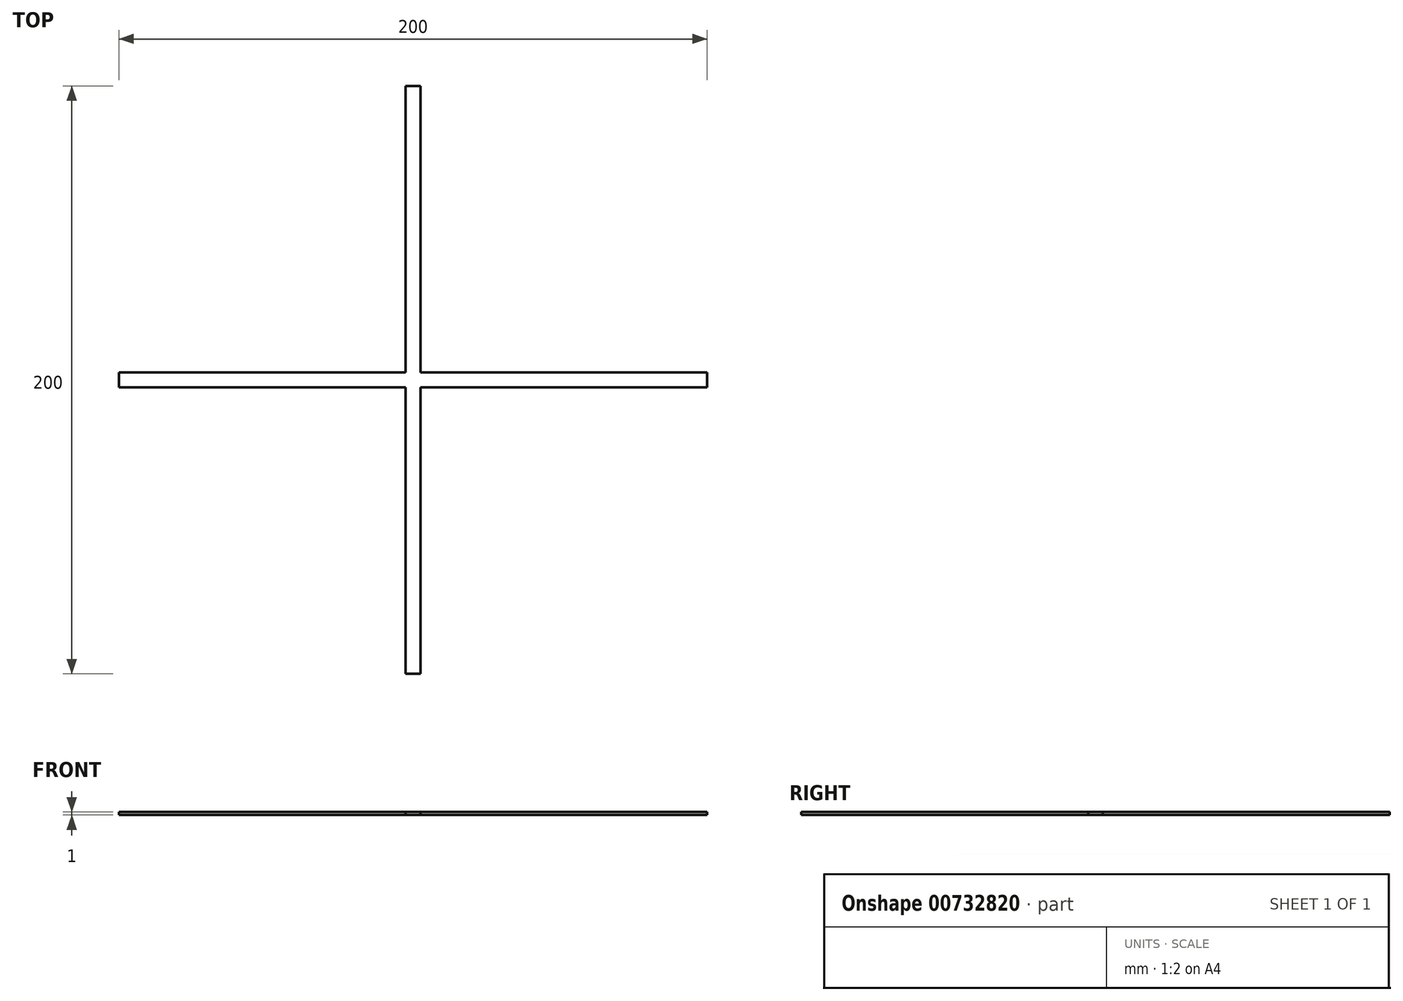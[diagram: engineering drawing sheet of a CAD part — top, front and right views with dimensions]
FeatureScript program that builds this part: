
annotation { "Feature Type Name" : "Feature", "Feature Type Description" : "" }
export const myFeature = defineFeature(function(context is Context, id is Id, definition is map)
    precondition{}
    {
        {
            var Q0;
            Q0=qCreatedBy(makeId("Top.planeOp"),FACE);
            var sketch = newSketch(context, id + "F0", { "sketchPlane" : qUnion([Q0])});
            skLineSegment(sketch, "E0.bottom", {"start": v(-100, 2.5) * mm, "end": v(100, 2.5) * mm});
            skLineSegment(sketch, "E0.top", {"start": v(-100, -2.5) * mm, "end": v(100, -2.5) * mm});
            skLineSegment(sketch, "E0.left", {"start": v(-100, 2.5) * mm, "end": v(-100, -2.5) * mm});
            skLineSegment(sketch, "E0.right", {"start": v(100, 2.5) * mm, "end": v(100, -2.5) * mm});
            skLineSegment(sketch, "E1.bottom", {"start": v(-2.5, 100) * mm, "end": v(2.5, 100) * mm});
            skLineSegment(sketch, "E1.top", {"start": v(-2.5, -100) * mm, "end": v(2.5, -100) * mm});
            skLineSegment(sketch, "E1.left", {"start": v(-2.5, 100) * mm, "end": v(-2.5, -100) * mm});
            skLineSegment(sketch, "E1.right", {"start": v(2.5, 100) * mm, "end": v(2.5, -100) * mm});
            skSolve(sketch);
        }
        {
            var Q0;
            Q0 = qSketchRegion(id + "F0", true);
            extrude(context, id + "F1", {"entities" : qUnion([Q0]), "depth" : 1 * mm, "offsetDistance" : 25 * mm});
        }
    });
